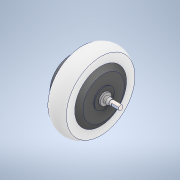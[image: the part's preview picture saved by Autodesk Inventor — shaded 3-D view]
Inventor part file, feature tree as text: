
AUTODESK INVENTOR PART (.ipt)
format: ipt  version: 2021 (Build 250183000, 183)  size: 204,800 bytes
history: mixed  units: in
note: dims shown in document units (in); Inventor stores cm internally (conversion verified against a paired STEP export)
features: extrude x2, sketch x2, other x1, imported_body x1
ambient origin geometry x8: Origin, YZ Plane, XZ Plane, XY Plane, X Axis, Y Axis, Z Axis, Center Point
bodies: Solid1 (imported_parasolid)
feature tree (6):
  extrude  "Extrusion1"  TaperAngle=0.0deg  [1 undecoded]
  extrude  "Extrusion2"  TaperAngle=0.0deg  [1 undecoded]
  sketch  "Sketch1"  dims[d0=0.3937in d1=0.0in]
  sketch  "Sketch2"  dims[d2=0.3937in d3=0.0in d4=0.2362in d5=0.2362in d6=0.75in d7=0.0in d8=0.3937in d9=0.0in d10=0.3937in d11=0.0in d12=0.2362in d13=0.2362in d14=0.75in d15=0.0in]
  other  "Boss-Extrude2"
  imported_body  NMx_Import_Brep_tag  [imported B-rep: ~36 faces, bbox_mm=[163.4, 57.35, 119.677417]]
note: 2 required parameter values undecoded (feature->parameter linkage not recoverable at this tier; creation-order binding heuristic only, values carry confidence <= 0.55)
